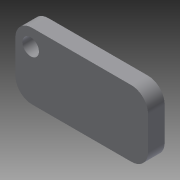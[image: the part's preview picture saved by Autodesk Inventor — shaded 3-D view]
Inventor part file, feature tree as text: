
AUTODESK INVENTOR PART (.ipt)
format: ipt  version: 2014 (Build 180170000, 170)  size: 87,552 bytes
history: native  units: in
note: dims shown in document units (in); Inventor stores cm internally (conversion verified against a paired STEP export)
features: extrude x1, hole x1, fillet x1, sketch x1
ambient origin geometry x8: Origin, YZ Plane, XZ Plane, XY Plane, X Axis, Y Axis, Z Axis, Center Point
bodies: Solid1 (feature_tree)
feature tree (4):
  extrude  "Extrusion1"  Depth=0.5in
  hole  "Hole1"  [1 undecoded]
  fillet  "Fillet1"  Radius=0.125in
  sketch  "Sketch1"  dims[d0=1.0in d1=0.5in d2=0.125in d3=0.0in d13=1.0in d14=1.0in d6=0.125in d7=0.75in d8=0.375in d9=0.25in d10=0.5635in d11=0.125in d12=0.8108in d15=0.125in d4=1.0in d5=1.0in]
note: 1 required parameter value undecoded (feature->parameter linkage not recoverable at this tier; creation-order binding heuristic only, values carry confidence <= 0.55)
